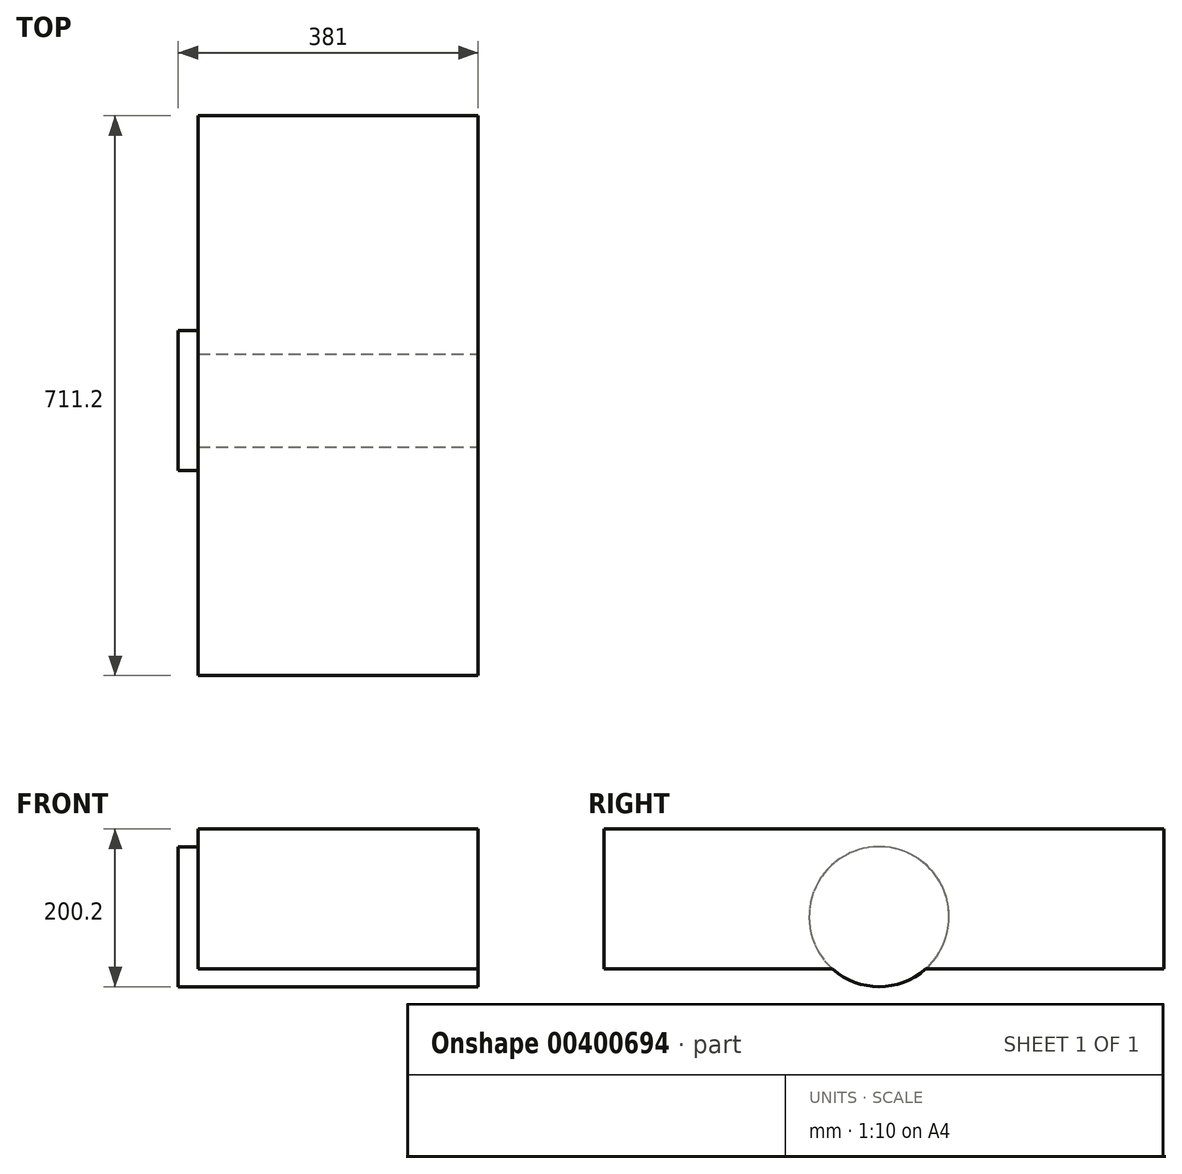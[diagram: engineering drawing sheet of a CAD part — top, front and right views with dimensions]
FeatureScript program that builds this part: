
annotation { "Feature Type Name" : "Feature", "Feature Type Description" : "" }
export const myFeature = defineFeature(function(context is Context, id is Id, definition is map)
    precondition{}
    {
        {
            var Q0;
            Q0=qCreatedBy(makeId("Top.planeOp"),FACE);
            var sketch = newSketch(context, id + "F0", { "sketchPlane" : qUnion([Q0])});
            skLineSegment(sketch, "E0.bottom", {"start": v(0, 0) * mm, "end": v(-355.6, 0) * mm});
            skLineSegment(sketch, "E0.top", {"start": v(0, 711.2) * mm, "end": v(-355.6, 711.2) * mm});
            skLineSegment(sketch, "E0.left", {"start": v(0, 0) * mm, "end": v(0, 711.2) * mm});
            skLineSegment(sketch, "E0.right", {"start": v(-355.6, 0) * mm, "end": v(-355.6, 711.2) * mm});
            skSolve(sketch);
        }
        {
            var Q0;
            Q0=makeQuery(id+"F0.imprint","IMPRINT",FACE,{"disambiguationData":[TD([[makeQuery(id+"F0.imprint","IMPRINT",EDGE,{"derivedFrom":sQuery(id+"F0.wireOp",EDGE,"E0.bottom")}),-1.0]])]});
            extrude(context, id + "F1", {"entities" : qUnion([Q0]), "oppositeDirection" : true, "depth" : 177.8 * mm});
        }
        {
            var Q0;
            Q0=makeQuery(id+"F1.opExtrude","SWEPT_FACE",FACE,{"disambiguationData":[OSD([sQuery(id+"F0.wireOp",EDGE,"E0.right")])]});
            var sketch = newSketch(context, id + "F2", { "sketchPlane" : qUnion([Q0])});
            skCircle(sketch, "E1", {"center": v(-349.33, -111.3) * mm, "radius": 88.9 * mm});
            skSolve(sketch);
        }
        {
            var Q0;
            {var subQ0=sQuery(id+"F2.wireOp",EDGE,"E1");var subQ1=makeQuery(id+"F1.opExtrude","CAP_EDGE",EDGE,{"disambiguationData":[OSD([sQuery(id+"F0.wireOp",EDGE,"E0.right")])],"isStart":false});var subQ2=makeQuery(id+"F2.imprint","INTERSECT",VERTEX,{"disambiguationData":[OD(0.0)],"derivedFrom":[subQ1,subQ0]});Q0=makeQuery(id+"F2.imprint","IMPRINT",FACE,{"disambiguationData":[TD([[makeQuery(id+"F2.imprint","IMPRINT",EDGE,{"disambiguationData":[TD([[subQ2,-1.0]])],"derivedFrom":subQ0}),1.0]])]});}
            var Q1;
            {var subQ0=sQuery(id+"F2.wireOp",EDGE,"E1");var subQ1=makeQuery(id+"F1.opExtrude","CAP_EDGE",EDGE,{"disambiguationData":[OSD([sQuery(id+"F0.wireOp",EDGE,"E0.right")])],"isStart":false});var subQ2=makeQuery(id+"F2.imprint","INTERSECT",VERTEX,{"disambiguationData":[OD(0.0)],"derivedFrom":[subQ1,subQ0]});Q1=makeQuery(id+"F2.imprint","IMPRINT",FACE,{"disambiguationData":[TD([[makeQuery(id+"F2.imprint","IMPRINT",EDGE,{"disambiguationData":[TD([[subQ2,1.0]])],"derivedFrom":subQ0}),1.0]])]});}
            var Q2;
            Q2=makeQuery(id+"F1.opExtrude","SWEPT_FACE",FACE,{"disambiguationData":[OSD([sQuery(id+"F0.wireOp",EDGE,"E0.left")])]});
            extrude(context, id + "F3", {"entities" : qUnion([Q0, Q1]), "operationType" : NewBodyOperationType.ADD, "depth" : 25.4 * mm, "hasSecondDirection" : true, "secondDirectionBound" : SecondDirectionBoundingType.UP_TO_SURFACE, "secondDirectionOppositeDirection" : true, "secondDirectionBoundEntityFace" : qUnion([Q2]), "secondDirectionDepth" : 25.4 * mm});
        }
    });
